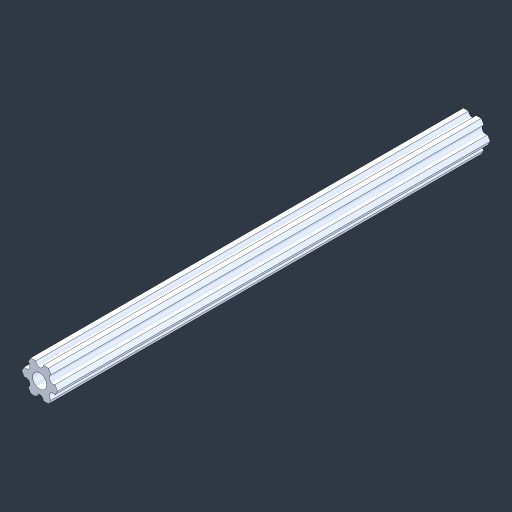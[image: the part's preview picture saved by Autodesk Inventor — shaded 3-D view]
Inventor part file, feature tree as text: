
AUTODESK INVENTOR PART (.ipt)
format: ipt  version: 2024.3 (Build 283343000, 343)  size: 105,984 bytes
history: native  units: mm (DEFAULTED — no unit token found)
features: extrude x1, sketch x1, other x1
ambient origin geometry x8: Origin, YZ Plane, XZ Plane, XY Plane, X Axis, Y Axis, Z Axis, Center Point
bodies: Solid1 (feature_tree)
feature tree (3):
  extrude  "Extrusion1"  [1 undecoded]
  sketch  "Sketch1"  dims[d0=177.8mm d1=0.0mm]
  other  "Boss-Extrude1"
note: 1 required parameter value undecoded (feature->parameter linkage not recoverable at this tier; creation-order binding heuristic only, values carry confidence <= 0.55)
